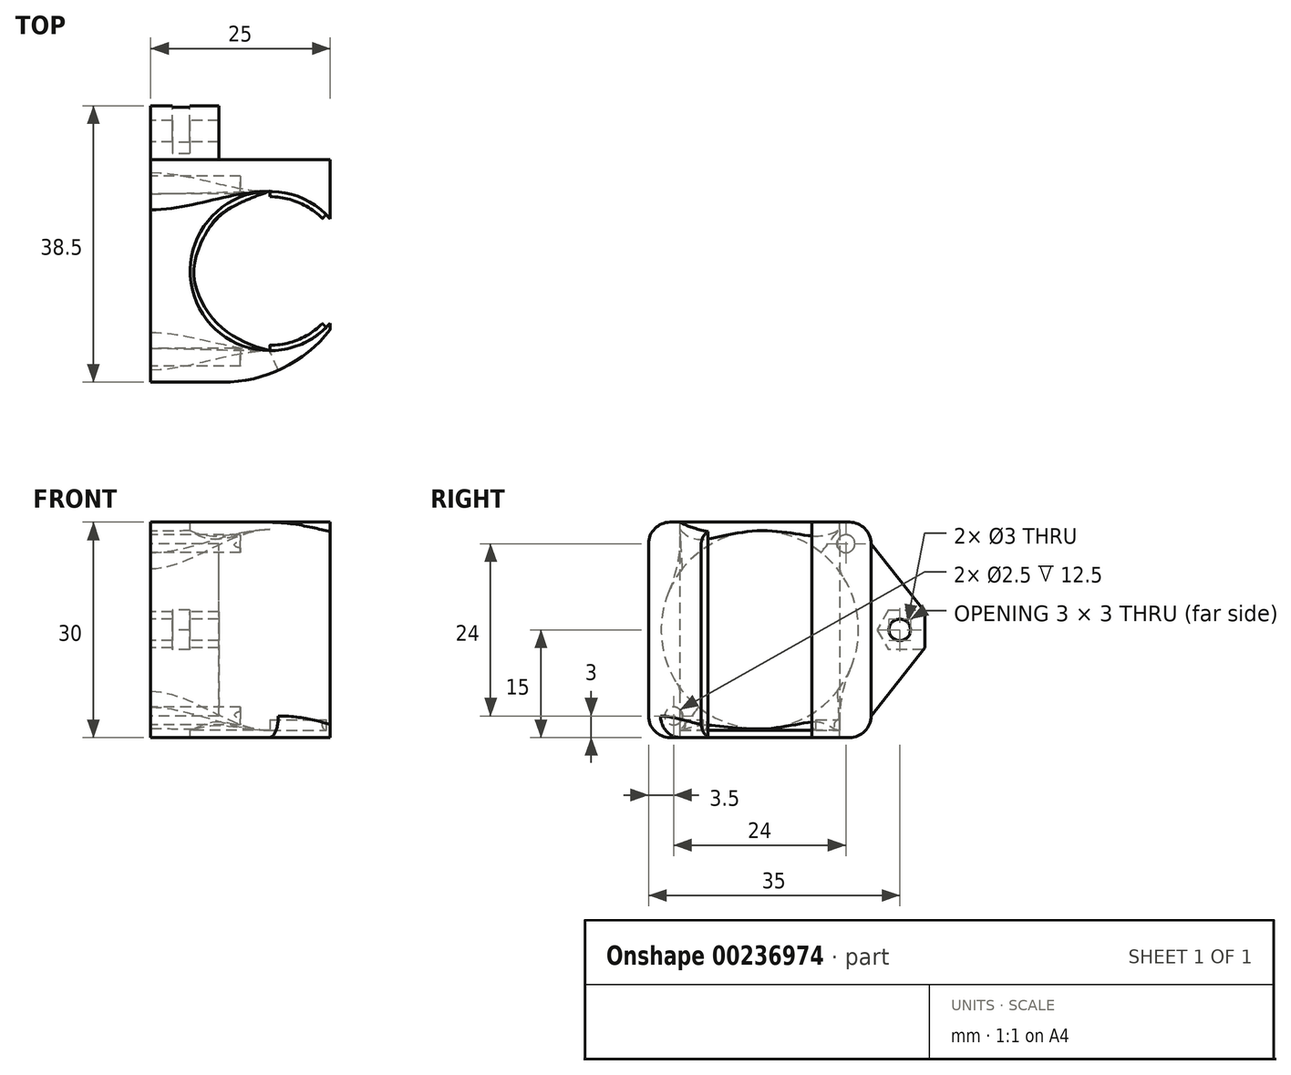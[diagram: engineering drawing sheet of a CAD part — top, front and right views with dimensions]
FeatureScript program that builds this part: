
annotation { "Feature Type Name" : "Feature", "Feature Type Description" : "" }
export const myFeature = defineFeature(function(context is Context, id is Id, definition is map)
    precondition{}
    {
        {
            var Q0;
            Q0=qCreatedBy(makeId("Right.planeOp"),FACE);
            var sketch = newSketch(context, id + "F0", { "sketchPlane" : qUnion([Q0])});
            skLineSegment(sketch, "E0.bottom", {"start": v(-15.5, -15) * mm, "end": v(15.5, -15) * mm});
            skLineSegment(sketch, "E0.top", {"start": v(-15.5, 15) * mm, "end": v(15.5, 15) * mm});
            skLineSegment(sketch, "E0.left", {"start": v(-15.5, -15) * mm, "end": v(-15.5, 15) * mm});
            skLineSegment(sketch, "E0.right", {"start": v(15.5, -15) * mm, "end": v(15.5, 15) * mm});
            skCircle(sketch, "E1", {"center": v(-12, -12) * mm, "radius": 1.25 * mm});
            skCircle(sketch, "E2", {"center": v(12, -12) * mm, "radius": 1.25 * mm});
            skCircle(sketch, "E3", {"center": v(12, 12) * mm, "radius": 1.25 * mm});
            skCircle(sketch, "E4", {"center": v(-12, 12) * mm, "radius": 1.25 * mm});
            skLineSegment(sketch, "E5", {"start": v(23, 2.5) * mm, "end": v(23, -2.5) * mm});
            skCircle(sketch, "E6", {"center": v(19.5, 0) * mm, "radius": 1.5 * mm});
            skCircle(sketch, "E7", {"center": v(0, 0) * mm, "radius": 13.75 * mm});
            skLineSegment(sketch, "E8", {"start": v(23, 2.5) * mm, "end": v(15.5, 12) * mm});
            skLineSegment(sketch, "E9", {"start": v(23, -2.5) * mm, "end": v(15.5, -12) * mm});
            skSolve(sketch);
        }
        {
            var Q0;
            Q0=makeQuery(id+"F0.imprint","IMPRINT",FACE,{"disambiguationData":[TD([[makeQuery(id+"F0.imprint","IMPRINT",EDGE,{"derivedFrom":sQuery(id+"F0.wireOp",EDGE,"E0.bottom")}),1.0]])]});
            var Q1;
            Q1=makeQuery(id+"F0.imprint","IMPRINT",FACE,{"disambiguationData":[TD([[makeQuery(id+"F0.imprint","IMPRINT",EDGE,{"derivedFrom":sQuery(id+"F0.wireOp",EDGE,"E7")}),1.0]])]});
            var Q2;
            Q2=makeQuery(id+"F0.imprint","IMPRINT",FACE,{"disambiguationData":[TD([[makeQuery(id+"F0.imprint","IMPRINT",EDGE,{"derivedFrom":sQuery(id+"F0.wireOp",EDGE,"E3")}),1.0]])]});
            var Q3;
            Q3=makeQuery(id+"F0.imprint","IMPRINT",FACE,{"disambiguationData":[TD([[makeQuery(id+"F0.imprint","IMPRINT",EDGE,{"derivedFrom":sQuery(id+"F0.wireOp",EDGE,"E4")}),1.0]])]});
            var Q4;
            Q4=makeQuery(id+"F0.imprint","IMPRINT",FACE,{"disambiguationData":[TD([[makeQuery(id+"F0.imprint","IMPRINT",EDGE,{"derivedFrom":sQuery(id+"F0.wireOp",EDGE,"E2")}),1.0]])]});
            var Q5;
            Q5=makeQuery(id+"F0.imprint","IMPRINT",FACE,{"disambiguationData":[TD([[makeQuery(id+"F0.imprint","IMPRINT",EDGE,{"derivedFrom":sQuery(id+"F0.wireOp",EDGE,"E1")}),1.0]])]});
            extrude(context, id + "F1", {"entities" : qUnion([Q0, Q1, Q2, Q3, Q4, Q5]), "depth" : 25 * mm});
        }
        {
            var Q0;
            Q0=makeQuery(id+"F0.imprint","IMPRINT",FACE,{"disambiguationData":[TD([[makeQuery(id+"F0.imprint","IMPRINT",EDGE,{"derivedFrom":sQuery(id+"F0.wireOp",EDGE,"E0.right")}),-1.0]])]});
            extrude(context, id + "F2", {"entities" : qUnion([Q0]), "operationType" : NewBodyOperationType.ADD, "depth" : 9.5 * mm});
        }
        {
            var Q0;
            Q0=qCreatedBy(makeId("Top.planeOp"),FACE);
            var sketch = newSketch(context, id + "F3", { "sketchPlane" : qUnion([Q0])});
            skCircle(sketch, "E10", {"center": v(16.6, 0) * mm, "radius": 11.1 * mm});
            skSolve(sketch);
        }
        {
            var Q0;
            Q0=makeQuery(id+"F3.imprint","IMPRINT",FACE,{"disambiguationData":[TD([[makeQuery(id+"F3.imprint","IMPRINT",EDGE,{"derivedFrom":sQuery(id+"F3.wireOp",EDGE,"E10")}),1.0]])]});
            extrude(context, id + "F4", {"entities" : qUnion([Q0]), "operationType" : NewBodyOperationType.REMOVE, "endBound" : BoundingType.SYMMETRIC, "oppositeDirection" : true, "depth" : 42 * mm});
        }
        {
            var Q0;
            Q0=makeQuery(id+"F0.imprint","IMPRINT",FACE,{"disambiguationData":[TD([[makeQuery(id+"F0.imprint","IMPRINT",EDGE,{"derivedFrom":sQuery(id+"F0.wireOp",EDGE,"E3")}),1.0]])]});
            var Q1;
            Q1=makeQuery(id+"F0.imprint","IMPRINT",FACE,{"disambiguationData":[TD([[makeQuery(id+"F0.imprint","IMPRINT",EDGE,{"derivedFrom":sQuery(id+"F0.wireOp",EDGE,"E1")}),1.0]])]});
            extrude(context, id + "F5", {"entities" : qUnion([Q0, Q1]), "operationType" : NewBodyOperationType.REMOVE, "depth" : 12.5 * mm});
        }
        {
            var Q0;
            Q0=qCreatedBy(makeId("Top.planeOp"),FACE);
            var sketch = newSketch(context, id + "F6", { "sketchPlane" : qUnion([Q0])});
            skLineSegment(sketch, "E11.0", {"start": v(25, -15.5) * mm, "end": v(10, -15.5) * mm});
            skLineSegment(sketch, "E12.0", {"start": v(25, -15.5) * mm, "end": v(25, -8.16) * mm});
            skArc(sketch, "E13", {"start": v(10, -15.5) * mm, "mid": v(18.35, -13.57) * mm, "end": v(25, -8.16) * mm});
            skPoint(sketch, "E14.orphan", {"position": v(25, -7.26) * mm});
            skPoint(sketch, "E15.orphan", {"position": v(0, -15.5) * mm});
            skSolve(sketch);
        }
        {
            var Q0;
            Q0 = qSketchRegion(id + "F6", true);
            extrude(context, id + "F7", {"entities" : qUnion([Q0]), "operationType" : NewBodyOperationType.REMOVE, "endBound" : BoundingType.SYMMETRIC, "oppositeDirection" : true, "depth" : 50 * mm});
        }
        {
            var Q0;
            Q0=qCreatedBy(makeId("Front.planeOp"),FACE);
            var sketch = newSketch(context, id + "F8", { "sketchPlane" : qUnion([Q0])});
            skLineSegment(sketch, "E16", {"start": v(5.5, -14) * mm, "end": v(5.5, -12.5) * mm});
            skArc(sketch, "E17", {"start": v(5.5, -12.5) * mm, "mid": v(6.25, -13.25) * mm, "end": v(5.5, -14) * mm});
            skSolve(sketch);
        }
        {
            var Q0;
            Q0 = qSketchRegion(id + "F8", true);
            var Q1;
            Q1=makeQuery(id+"F4.boolean.opBoolean","COPY",FACE,{"derivedFrom":makeQuery(id+"F4.opExtrude","SWEPT_FACE",FACE,{"disambiguationData":[OSD([sQuery(id+"F3.wireOp",EDGE,"E10")])]})});
            revolve(context, id + "F9", {"operationType" : NewBodyOperationType.ADD, "entities" : qUnion([Q0]), "axis" : qUnion([Q1]), "revolveType" : RevolveType.SYMMETRIC, "angle" : 270 * degree});
        }
        {
            var Q0;
            Q0=makeQuery(id+"F1.opExtrude","SWEPT_EDGE",EDGE,{"disambiguationData":[OSD([sQuery(id+"F0.wireOp",EDGE,"E0.top"),sQuery(id+"F0.wireOp",EDGE,"E0.left")])]});
            var Q1;
            Q1=makeQuery(id+"F7.boolean.opBoolean","INTERSECT",EDGE,{"derivedFrom":[makeQuery(id+"F1.opExtrude","SWEPT_FACE",FACE,{"disambiguationData":[OSD([sQuery(id+"F0.wireOp",EDGE,"E0.top")])]}),makeQuery(id+"F7.opExtrude","SWEPT_FACE",FACE,{"disambiguationData":[OSD([sQuery(id+"F6.wireOp",EDGE,"E13")])]})]});
            var Q2;
            Q2=makeQuery(id+"F1.opExtrude","SWEPT_EDGE",EDGE,{"disambiguationData":[OSD([sQuery(id+"F0.wireOp",EDGE,"E0.bottom"),sQuery(id+"F0.wireOp",EDGE,"E0.left")])]});
            var Q3;
            Q3=makeQuery(id+"F7.boolean.opBoolean","INTERSECT",EDGE,{"derivedFrom":[makeQuery(id+"F1.opExtrude","SWEPT_FACE",FACE,{"disambiguationData":[OSD([sQuery(id+"F0.wireOp",EDGE,"E0.bottom")])]}),makeQuery(id+"F7.opExtrude","SWEPT_FACE",FACE,{"disambiguationData":[OSD([sQuery(id+"F6.wireOp",EDGE,"E13")])]})]});
            var Q4;
            Q4=makeQuery(id+"FfeNmope8XcIB1r_1.1.F7.boolean.opBoolean","INTERSECT",EDGE,{"derivedFrom":[makeQuery(id+"F1.opExtrude","SWEPT_FACE",FACE,{"disambiguationData":[OSD([sQuery(id+"F0.wireOp",EDGE,"E0.top")])]}),makeQuery(id+"FfeNmope8XcIB1r_1.1.F7.opExtrude","SWEPT_FACE",FACE,{"disambiguationData":[OSD([sQuery(id+"F6.wireOp",EDGE,"E13")])]})]});
            var Q5;
            Q5=makeQuery(id+"F2.boolean.opBoolean","SPLIT",EDGE,{"derivedFrom":makeQuery(id+"F1.opExtrude","SWEPT_EDGE",EDGE,{"disambiguationData":[OSD([sQuery(id+"F0.wireOp",EDGE,"E0.top"),sQuery(id+"F0.wireOp",EDGE,"E0.right"),sQuery(id+"F0.wireOp",EDGE,"4L013uuU-bvVk-6wEZ-lnOh-J9ZBc70rgdpE")])]})});
            var Q6;
            Q6=makeQuery(id+"FfeNmope8XcIB1r_1.1.F7.boolean.opBoolean","INTERSECT",EDGE,{"derivedFrom":[makeQuery(id+"F1.opExtrude","SWEPT_FACE",FACE,{"disambiguationData":[OSD([sQuery(id+"F0.wireOp",EDGE,"E0.bottom")])]}),makeQuery(id+"FfeNmope8XcIB1r_1.1.F7.opExtrude","SWEPT_FACE",FACE,{"disambiguationData":[OSD([sQuery(id+"F6.wireOp",EDGE,"E13")])]})]});
            var Q7;
            Q7=makeQuery(id+"F2.boolean.opBoolean","SPLIT",EDGE,{"derivedFrom":makeQuery(id+"F1.opExtrude","SWEPT_EDGE",EDGE,{"disambiguationData":[OSD([sQuery(id+"F0.wireOp",EDGE,"E0.bottom"),sQuery(id+"F0.wireOp",EDGE,"E0.right"),sQuery(id+"F0.wireOp",EDGE,"9i42498X-nuqJ-4soy-1IrQ-E29PidHW4qtT")])]})});
            fillet(context, id + "F10", {"entities" : qUnion([Q0, Q1, Q2, Q3, Q4, Q5, Q6, Q7]), "radius" : 3 * mm, "tangentPropagation" : true, "allowEdgeOverflow" : false});
        }
        {
            var Q0;
            {var subQ0=sQuery(id+"F0.wireOp",EDGE,"E0.right");Q0=makeQuery(id+"F2.boolean.opBoolean","MERGE",FACE,{"derivedFrom":[makeQuery(id+"F1.opExtrude","CAP_FACE",FACE,{"disambiguationData":[OSD([sQuery(id+"F0.wireOp",EDGE,"E0.bottom"),sQuery(id+"F0.wireOp",EDGE,"E0.top"),sQuery(id+"F0.wireOp",EDGE,"E0.left"),subQ0])],"isStart":true}),makeQuery(id+"F2.opExtrude","CAP_FACE",FACE,{"disambiguationData":[OSD([subQ0,sQuery(id+"F0.wireOp",EDGE,"E5"),sQuery(id+"F0.wireOp",EDGE,"E6"),sQuery(id+"F0.wireOp",EDGE,"E8"),sQuery(id+"F0.wireOp",EDGE,"E9")])],"isStart":true})]});}
            cPlane(context, id + "F11", {"entities" : qUnion([Q0]), "cplaneType" : CPlaneType.OFFSET, "offset" : 3 * mm, "oppositeDirection" : true, "width" : 150 * mm, "height" : 150 * mm});
        }
        {
            var Q0;
            Q0=qCreatedBy(id+"F11.planeOp",FACE);
            var sketch = newSketch(context, id + "F12", { "sketchPlane" : qUnion([Q0])});
            skCircle(sketch, "E18.0", {"center": v(-19.5, 0) * mm, "radius": 1.5 * mm, "construction": true});
            skCircle(sketch, "E19", {"center": v(-19.5, 0) * mm, "radius": 2.75 * mm, "construction": true});
            skLineSegment(sketch, "E20.1", {"start": v(-17.91, 2.75) * mm, "end": v(-16.32, 0) * mm});
            skLineSegment(sketch, "E20.2", {"start": v(-16.32, 0) * mm, "end": v(-17.91, -2.75) * mm});
            skPoint(sketch, "E20.0.midPoint", {"position": v(-19.5, 2.75) * mm});
            skLineSegment(sketch, "E21", {"start": v(-17.91, 2.75) * mm, "end": v(-24.69, 2.75) * mm});
            skLineSegment(sketch, "E22", {"start": v(-24.69, 2.75) * mm, "end": v(-24.69, -2.75) * mm});
            skLineSegment(sketch, "E23", {"start": v(-24.69, -2.75) * mm, "end": v(-17.91, -2.75) * mm});
            skSolve(sketch);
        }
        {
            var Q0;
            Q0=makeQuery(id+"F12.imprint","IMPRINT",FACE,{"disambiguationData":[TD([[makeQuery(id+"F12.imprint","IMPRINT",EDGE,{"derivedFrom":sQuery(id+"F12.wireOp",EDGE,"E20.1")}),-1.0]])]});
            extrude(context, id + "F13", {"entities" : qUnion([Q0]), "operationType" : NewBodyOperationType.REMOVE, "oppositeDirection" : true, "depth" : 2.4 * mm});
        }
        {
            var Q0;
            Q0=qCreatedBy(makeId("Right.planeOp"),FACE);
            cPlane(context, id + "F14", {"entities" : qUnion([Q0]), "cplaneType" : CPlaneType.OFFSET, "offset" : (5.5 + 11.1) * mm, "width" : 150 * mm, "height" : 150 * mm});
        }
        {
            var Q0;
            Q0=qCreatedBy(id+"F14.planeOp",FACE);
            var sketch = newSketch(context, id + "F15", { "sketchPlane" : qUnion([Q0])});
            skLineSegment(sketch, "E24.0", {"start": v(-11.1, -14) * mm, "end": v(11.1, -14) * mm});
            skLineSegment(sketch, "E25", {"start": v(-11.1, -14) * mm, "end": v(-11.1, 14) * mm});
            skLineSegment(sketch, "E26", {"start": v(11.1, 14) * mm, "end": v(11.1, -14) * mm});
            skLineSegment(sketch, "E27", {"start": v(-11.1, 14) * mm, "end": v(11.1, 14) * mm});
            skSolve(sketch);
        }
        {
            var Q1;
            Q1=makeQuery(id+"F0.imprint","IMPRINT",FACE,{"disambiguationData":[TD([[makeQuery(id+"F0.imprint","IMPRINT",EDGE,{"derivedFrom":sQuery(id+"F0.wireOp",EDGE,"E7")}),1.0]])]});
            var Q2;
            Q2=makeQuery(id+"F15.imprint","IMPRINT",FACE,{"disambiguationData":[TD([[makeQuery(id+"F15.imprint","IMPRINT",EDGE,{"derivedFrom":sQuery(id+"F15.wireOp",EDGE,"E24.0")}),1.0]])]});
            loft(context, id + "F16", {"operationType" : NewBodyOperationType.REMOVE, "startCondition" : LoftEndDerivativeType.NORMAL_TO_PROFILE, "startMagnitude" : 1, "endCondition" : LoftEndDerivativeType.NORMAL_TO_PROFILE, "endMagnitude" : 1, "sheetProfilesArray" : [{ "sheetProfileEntities" : qUnion([Q1]) }, { "sheetProfileEntities" : qUnion([Q2]) }]});
        }
    });
